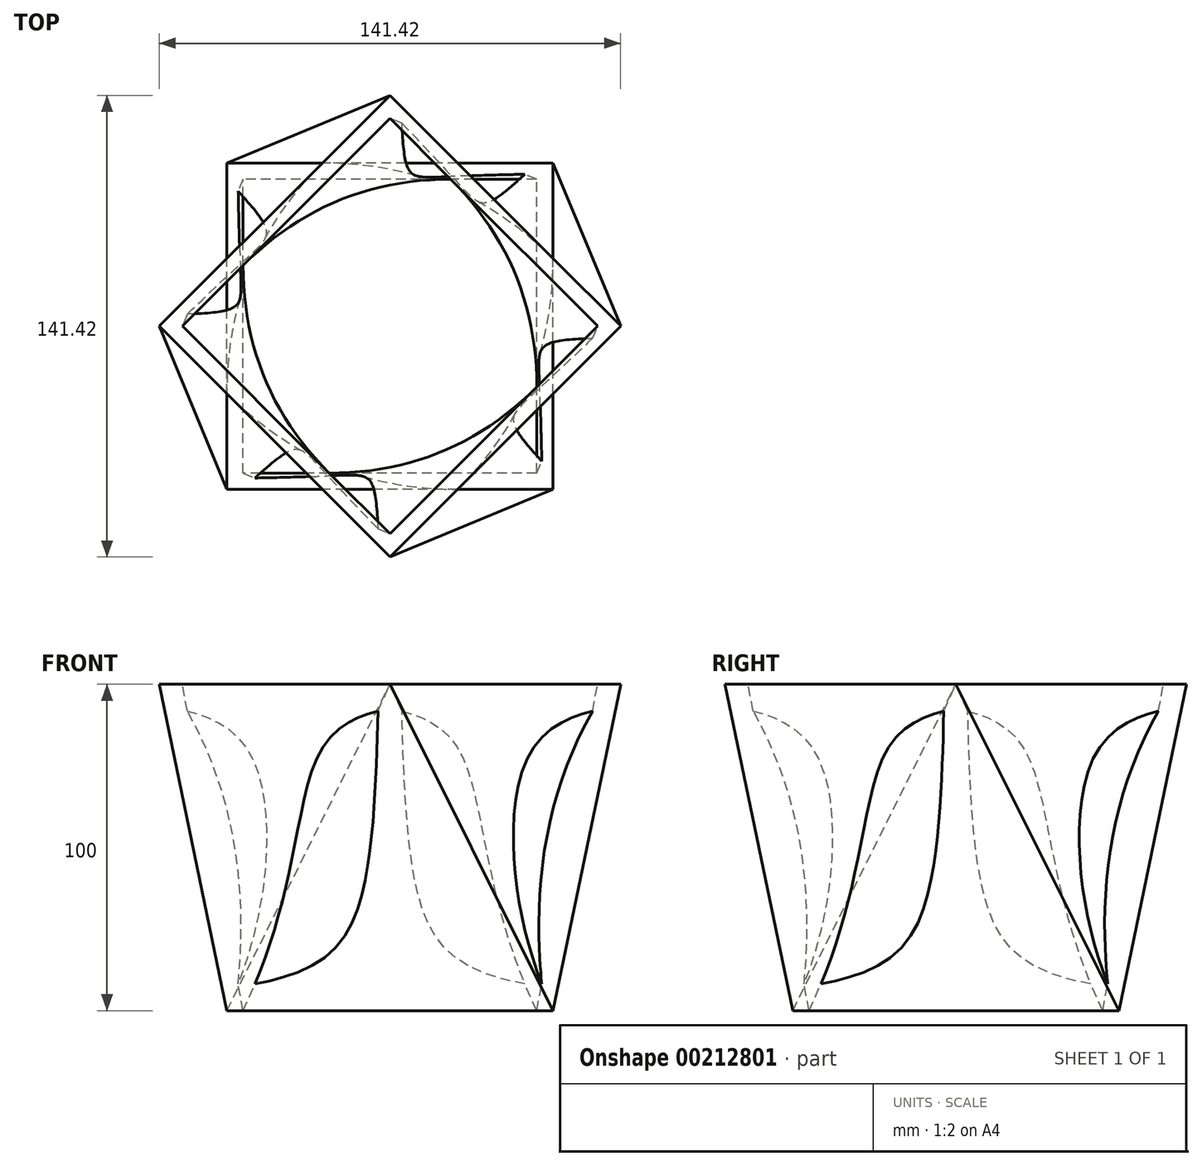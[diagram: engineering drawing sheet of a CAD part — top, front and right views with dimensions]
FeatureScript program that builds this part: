
annotation { "Feature Type Name" : "Feature", "Feature Type Description" : "" }
export const myFeature = defineFeature(function(context is Context, id is Id, definition is map)
    precondition{}
    {
        {
            var Q0;
            Q0=qCreatedBy(makeId("Top.planeOp"),FACE);
            var sketch = newSketch(context, id + "F0", { "sketchPlane" : qUnion([Q0])});
            skLineSegment(sketch, "E0.bottom", {"start": v(50, -50) * mm, "end": v(-50, -50) * mm});
            skLineSegment(sketch, "E0.top", {"start": v(50, 50) * mm, "end": v(-50, 50) * mm});
            skLineSegment(sketch, "E0.left", {"start": v(50, -50) * mm, "end": v(50, 50) * mm});
            skLineSegment(sketch, "E0.right", {"start": v(-50, -50) * mm, "end": v(-50, 50) * mm});
            skPoint(sketch, "E0.middle", {"position": v(0, 0) * mm});
            skSolve(sketch);
        }
        {
            var Q0;
            Q0=qCreatedBy(makeId("Top.planeOp"),FACE);
            cPlane(context, id + "F1", {"entities" : qUnion([Q0]), "cplaneType" : CPlaneType.OFFSET, "offset" : 100 * mm, "width" : 150 * mm, "height" : 150 * mm});
        }
        {
            var Q0;
            Q0=qCreatedBy(id+"F1.planeOp",FACE);
            var sketch = newSketch(context, id + "F2", { "sketchPlane" : qUnion([Q0])});
            skPoint(sketch, "E1.middle", {"position": v(0, 0) * mm});
            skCircle(sketch, "E2.cCircle", {"center": v(0, 0) * mm, "radius": 50 * mm, "construction": true});
            skLineSegment(sketch, "E2.0", {"start": v(70.71, 0) * mm, "end": v(0, -70.71) * mm});
            skLineSegment(sketch, "E2.1", {"start": v(0, -70.71) * mm, "end": v(-70.71, 0) * mm});
            skLineSegment(sketch, "E2.2", {"start": v(-70.71, 0) * mm, "end": v(0, 70.71) * mm});
            skLineSegment(sketch, "E2.3", {"start": v(0, 70.71) * mm, "end": v(70.71, 0) * mm});
            skPoint(sketch, "E2.0.midPoint", {"position": v(35.36, -35.36) * mm});
            skSolve(sketch);
        }
        {
            var Q0;
            Q0=makeQuery(id+"F0.imprint","IMPRINT",FACE,{"disambiguationData":[TD([[makeQuery(id+"F0.imprint","IMPRINT",EDGE,{"derivedFrom":sQuery(id+"F0.wireOp",EDGE,"E0.bottom")}),-1.0]])]});
            var Q1;
            Q1=makeQuery(id+"F2.imprint","IMPRINT",FACE,{"disambiguationData":[TD([[makeQuery(id+"F2.imprint","IMPRINT",EDGE,{"derivedFrom":sQuery(id+"F2.wireOp",EDGE,"E2.0")}),-1.0]])]});
            loft(context, id + "F3", {"sheetProfilesArray" : [{ "sheetProfileEntities" : qUnion([Q0]) }, { "sheetProfileEntities" : qUnion([Q1]) }]});
        }
        {
            var Q0;
            Q0=qCreatedBy(makeId("Top.planeOp"),FACE);
            var sketch = newSketch(context, id + "F4", { "sketchPlane" : qUnion([Q0])});
            skLineSegment(sketch, "E3.bottom", {"start": v(45, -45) * mm, "end": v(-45, -45) * mm});
            skLineSegment(sketch, "E3.top", {"start": v(45, 45) * mm, "end": v(-45, 45) * mm});
            skLineSegment(sketch, "E3.left", {"start": v(45, -45) * mm, "end": v(45, 45) * mm});
            skLineSegment(sketch, "E3.right", {"start": v(-45, -45) * mm, "end": v(-45, 45) * mm});
            skPoint(sketch, "E3.middle", {"position": v(0, 0) * mm});
            skSolve(sketch);
        }
        {
            var Q0;
            Q0=qCreatedBy(id+"F1.planeOp",FACE);
            var sketch = newSketch(context, id + "F5", { "sketchPlane" : qUnion([Q0])});
            skCircle(sketch, "E4.cCircle", {"center": v(0, 0) * mm, "radius": 45 * mm, "construction": true});
            skLineSegment(sketch, "E4.0", {"start": v(0, 63.64) * mm, "end": v(63.64, 0) * mm});
            skLineSegment(sketch, "E4.1", {"start": v(63.64, 0) * mm, "end": v(0, -63.64) * mm});
            skLineSegment(sketch, "E4.2", {"start": v(0, -63.64) * mm, "end": v(-63.64, 0) * mm});
            skLineSegment(sketch, "E4.3", {"start": v(-63.64, 0) * mm, "end": v(0, 63.64) * mm});
            skPoint(sketch, "E4.0.midPoint", {"position": v(31.82, 31.82) * mm});
            skSolve(sketch);
        }
        {
            var Q1;
            Q1=makeQuery(id+"F4.imprint","IMPRINT",FACE,{"disambiguationData":[TD([[makeQuery(id+"F4.imprint","IMPRINT",EDGE,{"derivedFrom":sQuery(id+"F4.wireOp",EDGE,"E3.bottom")}),-1.0]])]});
            var Q2;
            Q2=makeQuery(id+"F5.imprint","IMPRINT",FACE,{"disambiguationData":[TD([[makeQuery(id+"F5.imprint","IMPRINT",EDGE,{"derivedFrom":sQuery(id+"F5.wireOp",EDGE,"E4.0")}),-1.0]])]});
            var Q3;
            Q3=sQuery(id+"F4.wireOp",VERTEX,"E3.right.start");
            var Q4;
            Q4=sQuery(id+"F5.wireOp",VERTEX,"E4.2.start");
            loft(context, id + "F6", {"operationType" : NewBodyOperationType.REMOVE, "sheetProfilesArray" : [{ "sheetProfileEntities" : qUnion([Q1]) }, { "sheetProfileEntities" : qUnion([Q2]) }], "matchConnections" : true, "connections" : [{ "connectionEntities" : qUnion([Q3, Q4]), "connectionEdgeQueries" : qUnion([]), "connectionEdgeParameters" : [] }]});
        }
    });
